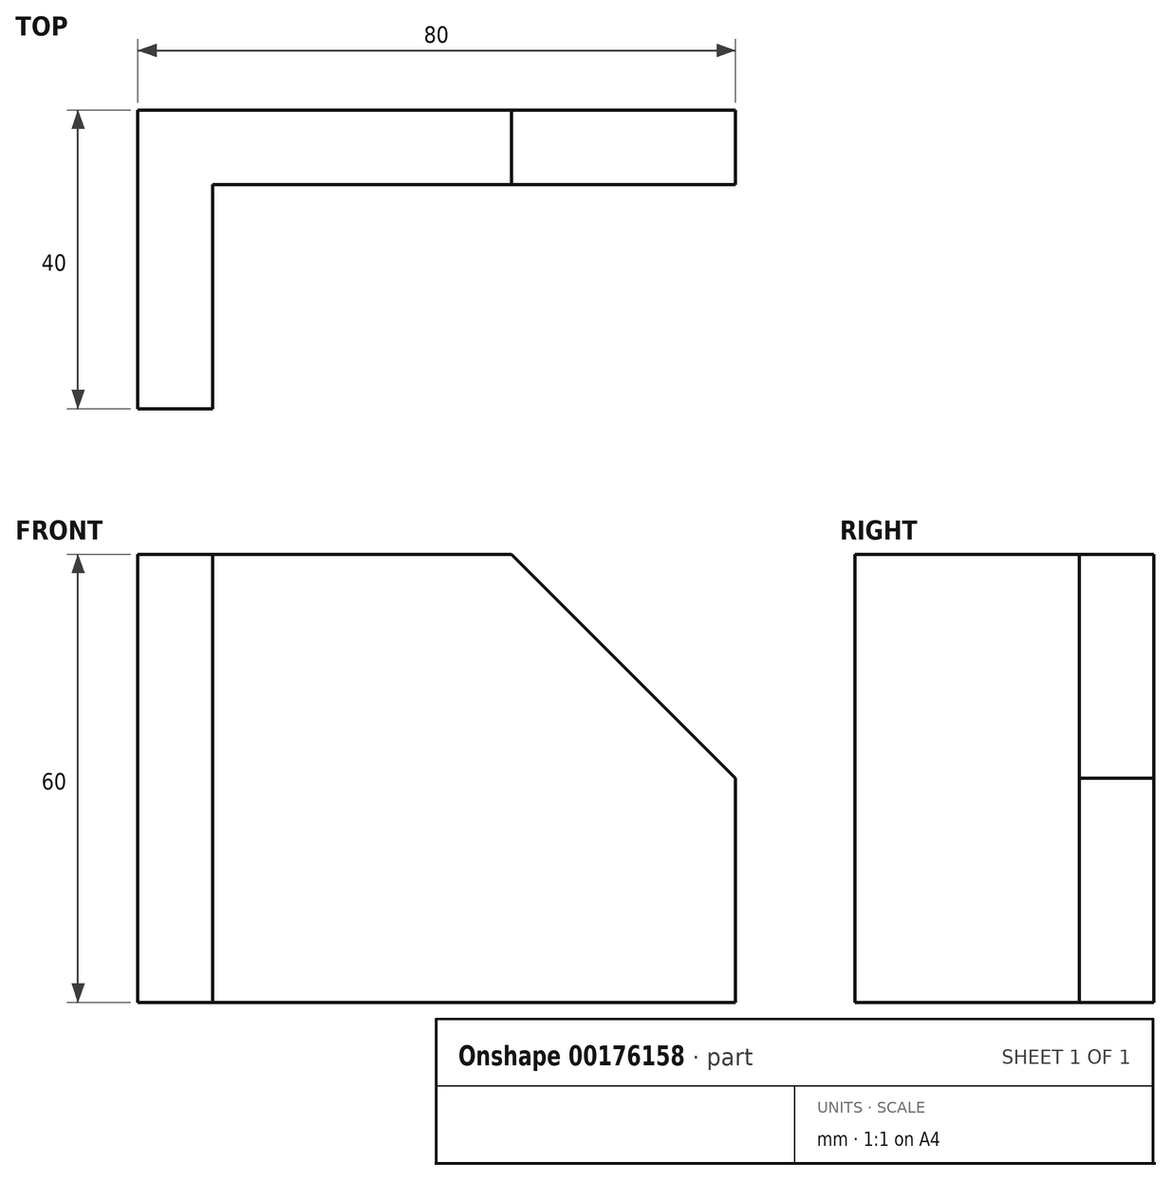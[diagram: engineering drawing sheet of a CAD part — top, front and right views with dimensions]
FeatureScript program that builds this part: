
annotation { "Feature Type Name" : "Feature", "Feature Type Description" : "" }
export const myFeature = defineFeature(function(context is Context, id is Id, definition is map)
    precondition{}
    {
        {
            var Q0;
            Q0=qCreatedBy(makeId("Front.planeOp"),FACE);
            var sketch = newSketch(context, id + "F0", { "sketchPlane" : qUnion([Q0])});
            skLineSegment(sketch, "E0.bottom", {"start": v(10, 30) * mm, "end": v(-40, 30) * mm});
            skLineSegment(sketch, "E0.top", {"start": v(40, -30) * mm, "end": v(-40, -30) * mm});
            skLineSegment(sketch, "E0.left", {"start": v(40, 0) * mm, "end": v(40, -30) * mm});
            skLineSegment(sketch, "E0.right", {"start": v(-40, 30) * mm, "end": v(-40, -30) * mm});
            skPoint(sketch, "E0.middle", {"position": v(0, 0) * mm});
            skLineSegment(sketch, "E1", {"start": v(10, 30) * mm, "end": v(40, 0) * mm});
            skPoint(sketch, "E2.orphan", {"position": v(40, 30) * mm});
            skLineSegment(sketch, "E3", {"start": v(-40, 30) * mm, "end": v(-30, 30) * mm});
            skSolve(sketch);
        }
        {
            var Q0;
            Q0=makeQuery(id+"F0.imprint","IMPRINT",FACE,{"disambiguationData":[TD([[makeQuery(id+"F0.imprint","IMPRINT",EDGE,{"derivedFrom":sQuery(id+"F0.wireOp",EDGE,"E0.bottom")}),1.0]])]});
            extrude(context, id + "F1", {"entities" : qUnion([Q0]), "depth" : 10 * mm});
        }
        {
            var Q0;
            Q0=makeQuery(id+"F1.opExtrude","CAP_FACE",FACE,{"disambiguationData":[OSD([sQuery(id+"F0.wireOp",EDGE,"E0.bottom"),sQuery(id+"F0.wireOp",EDGE,"E0.top"),sQuery(id+"F0.wireOp",EDGE,"E0.left"),sQuery(id+"F0.wireOp",EDGE,"E0.right"),sQuery(id+"F0.wireOp",EDGE,"E1"),sQuery(id+"F0.wireOp",EDGE,"E3")])],"isStart":false});
            var sketch = newSketch(context, id + "F2", { "sketchPlane" : qUnion([Q0])});
            skLineSegment(sketch, "E4", {"start": v(-30, 30) * mm, "end": v(-30, -30) * mm});
            skSolve(sketch);
        }
        {
            var Q0;
            Q0 = qSketchRegion(id + "F2", true);
            var Q1;
            {var subQ0=sQuery(id+"F2.wireOp",EDGE,"E4");Q1=makeQuery(id+"F2.imprint","IMPRINT",FACE,{"disambiguationData":[TD([[makeQuery(id+"F2.imprint","IMPRINT",EDGE,{"derivedFrom":subQ0}),-1.0]])]});}
            extrude(context, id + "F3", {"entities" : qUnion([Q0, Q1]), "operationType" : NewBodyOperationType.ADD, "depth" : 30 * mm});
        }
    });
